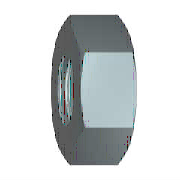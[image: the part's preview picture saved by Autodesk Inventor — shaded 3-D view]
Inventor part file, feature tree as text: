
AUTODESK INVENTOR PART (.ipt)
format: ipt  version: 2025 (Build 290162000, 162)  size: 175,616 bytes
history: native  units: mm (DEFAULTED — no unit token found)
features: chamfer x1, hole x1, other x1, plane x1
ambient origin geometry x7: Origin, YZ Plane, XZ Plane, X Axis, Y Axis, Z Axis, Center Point
bodies: Solid1 (feature_tree), Body (feature_tree)
feature tree (4):
  chamfer  "Chamfer1"  Distance=8.082904mm
  hole  "Thread"  [1 undecoded]
  other  "Work Axis1"
  plane  "Work Plane1"
note: 1 required parameter value undecoded (feature->parameter linkage not recoverable at this tier; creation-order binding heuristic only, values carry confidence <= 0.55)
